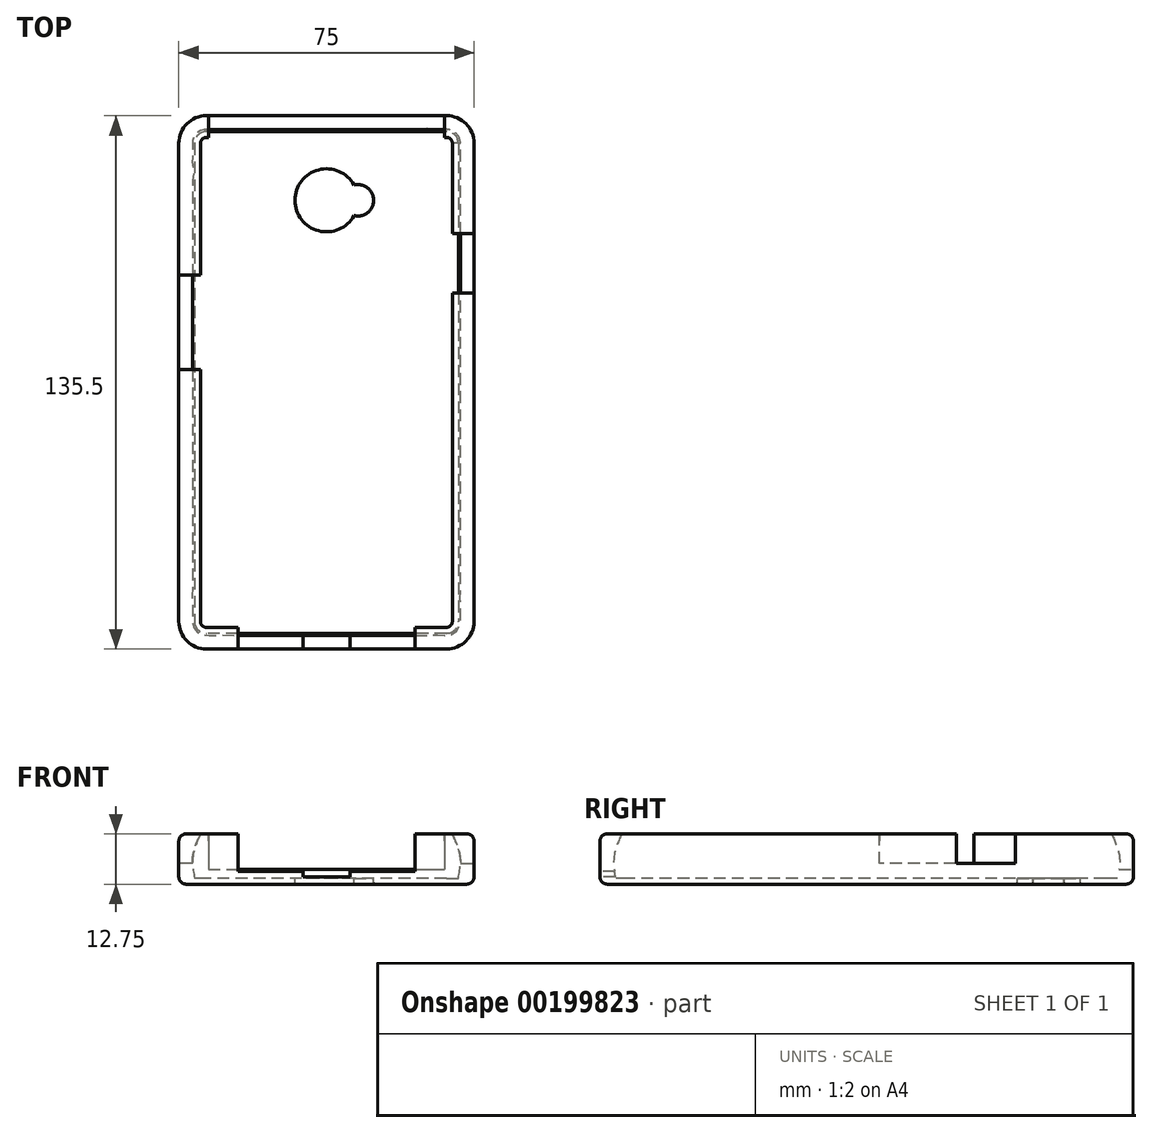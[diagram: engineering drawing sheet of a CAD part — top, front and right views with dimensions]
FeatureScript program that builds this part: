
annotation { "Feature Type Name" : "Feature", "Feature Type Description" : "" }
export const myFeature = defineFeature(function(context is Context, id is Id, definition is map)
    precondition{}
    {
        {
            var Q0;
            Q0=qCreatedBy(makeId("Top.planeOp"),FACE);
            var sketch = newSketch(context, id + "F0", { "sketchPlane" : qUnion([Q0])});
            skLineSegment(sketch, "E0.bottom", {"start": v(30.5, 63.25) * mm, "end": v(-30.5, 63.25) * mm});
            skLineSegment(sketch, "E0.top", {"start": v(30.5, -63.25) * mm, "end": v(-30.5, -63.25) * mm});
            skLineSegment(sketch, "E0.left", {"start": v(33, 60.75) * mm, "end": v(33, -60.75) * mm});
            skLineSegment(sketch, "E0.right", {"start": v(-33, 60.75) * mm, "end": v(-33, -60.75) * mm});
            skPoint(sketch, "E0.middle", {"position": v(0, 0) * mm});
            skPoint(sketch, "E1.visualSharp", {"position": v(-33, 63.25) * mm});
            skArc(sketch, "E1.filletArc", {"start": v(-30.5, 63.25) * mm, "mid": v(-32.27, 62.52) * mm, "end": v(-33, 60.75) * mm});
            skPoint(sketch, "E2.visualSharp", {"position": v(33, 63.25) * mm});
            skArc(sketch, "E2.filletArc", {"start": v(33, 60.75) * mm, "mid": v(32.27, 62.52) * mm, "end": v(30.5, 63.25) * mm});
            skPoint(sketch, "E3.visualSharp", {"position": v(33, -63.25) * mm});
            skArc(sketch, "E3.filletArc", {"start": v(30.5, -63.25) * mm, "mid": v(32.27, -62.52) * mm, "end": v(33, -60.75) * mm});
            skPoint(sketch, "E4.visualSharp", {"position": v(-33, -63.25) * mm});
            skArc(sketch, "E4.filletArc", {"start": v(-33, -60.75) * mm, "mid": v(-32.27, -62.52) * mm, "end": v(-30.5, -63.25) * mm});
            skArc(sketch, "E5.0", {"start": v(37.5, 60.75) * mm, "mid": v(35.45, 65.7) * mm, "end": v(30.5, 67.75) * mm});
            skLineSegment(sketch, "E5.1", {"start": v(37.5, 60.75) * mm, "end": v(37.5, -60.75) * mm});
            skLineSegment(sketch, "E5.2", {"start": v(30.5, 67.75) * mm, "end": v(-30.5, 67.75) * mm});
            skArc(sketch, "E5.3", {"start": v(30.5, -67.75) * mm, "mid": v(35.45, -65.7) * mm, "end": v(37.5, -60.75) * mm});
            skArc(sketch, "E5.4", {"start": v(-30.5, 67.75) * mm, "mid": v(-35.45, 65.7) * mm, "end": v(-37.5, 60.75) * mm});
            skLineSegment(sketch, "E5.5", {"start": v(-37.5, 60.75) * mm, "end": v(-37.5, -60.75) * mm});
            skArc(sketch, "E5.6", {"start": v(-37.5, -60.75) * mm, "mid": v(-35.45, -65.7) * mm, "end": v(-30.5, -67.75) * mm});
            skLineSegment(sketch, "E5.7", {"start": v(30.5, -67.75) * mm, "end": v(-30.5, -67.75) * mm});
            skSolve(sketch);
        }
        {
            var Q0;
            Q0=makeQuery(id+"F0.imprint","IMPRINT",FACE,{"disambiguationData":[TD([[makeQuery(id+"F0.imprint","IMPRINT",EDGE,{"derivedFrom":sQuery(id+"F0.wireOp",EDGE,"E0.bottom")}),-1.0]])]});
            var Q1;
            Q1=makeQuery(id+"F0.imprint","IMPRINT",FACE,{"disambiguationData":[TD([[makeQuery(id+"F0.imprint","IMPRINT",EDGE,{"derivedFrom":sQuery(id+"F0.wireOp",EDGE,"E0.bottom")}),1.0]])]});
            extrude(context, id + "F1", {"entities" : qUnion([Q0, Q1]), "depth" : 12.75 * mm});
        }
        {
            var Q0;
            Q0=qCreatedBy(makeId("Top.planeOp"),FACE);
            cPlane(context, id + "F2", {"entities" : qUnion([Q0]), "cplaneType" : CPlaneType.OFFSET, "offset" : 1.5 * mm, "width" : 150 * mm, "height" : 150 * mm});
        }
        {
            var Q0;
            Q0=qCreatedBy(id+"F2.planeOp",FACE);
            var sketch = newSketch(context, id + "F3", { "sketchPlane" : qUnion([Q0])});
            skArc(sketch, "E6.0", {"start": v(33.5, 60.75) * mm, "mid": v(32.62, 62.87) * mm, "end": v(30.5, 63.75) * mm});
            skLineSegment(sketch, "E6.1", {"start": v(33.5, 60.75) * mm, "end": v(33.5, -60.75) * mm});
            skLineSegment(sketch, "E6.2", {"start": v(30.5, 63.75) * mm, "end": v(-30.5, 63.75) * mm});
            skArc(sketch, "E6.3", {"start": v(30.5, -63.75) * mm, "mid": v(32.62, -62.87) * mm, "end": v(33.5, -60.75) * mm});
            skArc(sketch, "E6.4", {"start": v(-30.5, 63.75) * mm, "mid": v(-32.62, 62.87) * mm, "end": v(-33.5, 60.75) * mm});
            skLineSegment(sketch, "E6.5", {"start": v(-33.5, 60.75) * mm, "end": v(-33.5, -60.75) * mm});
            skArc(sketch, "E6.6", {"start": v(-33.5, -60.75) * mm, "mid": v(-32.62, -62.87) * mm, "end": v(-30.5, -63.75) * mm});
            skLineSegment(sketch, "E6.7", {"start": v(30.5, -63.75) * mm, "end": v(-30.5, -63.75) * mm});
            skSolve(sketch);
        }
        {
            var Q0;
            Q0=qCreatedBy(id+"F2.planeOp",FACE);
            cPlane(context, id + "F4", {"entities" : qUnion([Q0]), "cplaneType" : CPlaneType.OFFSET, "offset" : 5 * mm, "width" : 150 * mm, "height" : 150 * mm});
        }
        {
            var Q0;
            Q0=qCreatedBy(id+"F4.planeOp",FACE);
            var sketch = newSketch(context, id + "F5", { "sketchPlane" : qUnion([Q0])});
            skArc(sketch, "E7.0", {"start": v(34, 60.75) * mm, "mid": v(32.97, 63.22) * mm, "end": v(30.5, 64.25) * mm});
            skLineSegment(sketch, "E7.1", {"start": v(34, 60.75) * mm, "end": v(34, -60.75) * mm});
            skLineSegment(sketch, "E7.2", {"start": v(30.5, 64.25) * mm, "end": v(-30.5, 64.25) * mm});
            skArc(sketch, "E7.3", {"start": v(30.5, -64.25) * mm, "mid": v(32.97, -63.22) * mm, "end": v(34, -60.75) * mm});
            skArc(sketch, "E7.4", {"start": v(-30.5, 64.25) * mm, "mid": v(-32.97, 63.22) * mm, "end": v(-34, 60.75) * mm});
            skLineSegment(sketch, "E7.5", {"start": v(-34, 60.75) * mm, "end": v(-34, -60.75) * mm});
            skArc(sketch, "E7.6", {"start": v(-34, -60.75) * mm, "mid": v(-32.97, -63.22) * mm, "end": v(-30.5, -64.25) * mm});
            skLineSegment(sketch, "E7.7", {"start": v(30.5, -64.25) * mm, "end": v(-30.5, -64.25) * mm});
            skSolve(sketch);
        }
        {
            var Q0;
            Q0=makeQuery(id+"F1.opExtrude","CAP_FACE",FACE,{"disambiguationData":[OSD([sQuery(id+"F0.wireOp",EDGE,"E5.0"),sQuery(id+"F0.wireOp",EDGE,"E5.1"),sQuery(id+"F0.wireOp",EDGE,"E5.2"),sQuery(id+"F0.wireOp",EDGE,"E5.3"),sQuery(id+"F0.wireOp",EDGE,"E5.4"),sQuery(id+"F0.wireOp",EDGE,"E5.5"),sQuery(id+"F0.wireOp",EDGE,"E5.6"),sQuery(id+"F0.wireOp",EDGE,"E5.7")])],"isStart":false});
            var sketch = newSketch(context, id + "F6", { "sketchPlane" : qUnion([Q0])});
            skArc(sketch, "E8.0", {"start": v(32, 60.75) * mm, "mid": v(31.56, 61.81) * mm, "end": v(30.5, 62.25) * mm});
            skLineSegment(sketch, "E8.1", {"start": v(32, 60.75) * mm, "end": v(32, -60.75) * mm});
            skLineSegment(sketch, "E8.2", {"start": v(30.5, 62.25) * mm, "end": v(-30.5, 62.25) * mm});
            skArc(sketch, "E8.3", {"start": v(30.5, -62.25) * mm, "mid": v(31.56, -61.81) * mm, "end": v(32, -60.75) * mm});
            skArc(sketch, "E8.4", {"start": v(-30.5, 62.25) * mm, "mid": v(-31.56, 61.81) * mm, "end": v(-32, 60.75) * mm});
            skLineSegment(sketch, "E8.5", {"start": v(-32, 60.75) * mm, "end": v(-32, -60.75) * mm});
            skArc(sketch, "E8.6", {"start": v(-32, -60.75) * mm, "mid": v(-31.56, -61.81) * mm, "end": v(-30.5, -62.25) * mm});
            skLineSegment(sketch, "E8.7", {"start": v(30.5, -62.25) * mm, "end": v(-30.5, -62.25) * mm});
            skSolve(sketch);
        }
        {
            var Q1;
            Q1=makeQuery(id+"F3.imprint","IMPRINT",FACE,{"disambiguationData":[TD([[makeQuery(id+"F3.imprint","IMPRINT",EDGE,{"derivedFrom":sQuery(id+"F3.wireOp",EDGE,"E6.0")}),1.0]])]});
            var Q2;
            Q2=makeQuery(id+"F5.imprint","IMPRINT",FACE,{"disambiguationData":[TD([[makeQuery(id+"F5.imprint","IMPRINT",EDGE,{"derivedFrom":sQuery(id+"F5.wireOp",EDGE,"E7.0")}),1.0]])]});
            var Q3;
            Q3=makeQuery(id+"F6.imprint","IMPRINT",FACE,{"disambiguationData":[TD([[makeQuery(id+"F6.imprint","IMPRINT",EDGE,{"derivedFrom":sQuery(id+"F6.wireOp",EDGE,"E8.0")}),1.0]])]});
            loft(context, id + "F7", {"operationType" : NewBodyOperationType.REMOVE, "sheetProfilesArray" : [{ "sheetProfileEntities" : qUnion([Q1]) }, { "sheetProfileEntities" : qUnion([Q2]) }, { "sheetProfileEntities" : qUnion([Q3]) }]});
        }
        {
            var Q0;
            Q0=makeQuery(id+"F7.boolean.opBoolean","COPY",FACE,{"derivedFrom":makeQuery(id+"F7.opLoft","CAP_FACE",FACE,{"disambiguationData":[OSD([makeQuery(id+"F3.imprint","IMPRINT",FACE,{"disambiguationData":[TD([[makeQuery(id+"F3.imprint","IMPRINT",EDGE,{"derivedFrom":sQuery(id+"F3.wireOp",EDGE,"E6.0")}),1.0]])]})])],"isStart":true})});
            var sketch = newSketch(context, id + "F8", { "sketchPlane" : qUnion([Q0])});
            skArc(sketch, "E9", {"start": v(7, 50.12) * mm, "mid": v(-8, 46.25) * mm, "end": v(7, 42.38) * mm});
            skArc(sketch, "E10", {"start": v(7, 42.38) * mm, "mid": v(12, 46.25) * mm, "end": v(7, 50.12) * mm});
            skSolve(sketch);
        }
        {
            var Q0;
            Q0=makeQuery(id+"F8.imprint","IMPRINT",FACE,{"disambiguationData":[TD([[makeQuery(id+"F8.imprint","IMPRINT",EDGE,{"derivedFrom":sQuery(id+"F8.wireOp",EDGE,"E9")}),1.0]])]});
            extrude(context, id + "F9", {"entities" : qUnion([Q0]), "operationType" : NewBodyOperationType.REMOVE, "oppositeDirection" : true, "depth" : 5 * mm});
        }
        {
            var Q0;
            Q0=makeQuery(id+"F1.opExtrude","SWEPT_FACE",FACE,{"disambiguationData":[OSD([sQuery(id+"F0.wireOp",EDGE,"E5.5")])]});
            var sketch = newSketch(context, id + "F10", { "sketchPlane" : qUnion([Q0])});
            skLineSegment(sketch, "E11.bottom", {"start": v(-27.25, 5.25) * mm, "end": v(-3.25, 5.25) * mm});
            skLineSegment(sketch, "E11.top", {"start": v(-27.25, 12.75) * mm, "end": v(-3.25, 12.75) * mm});
            skLineSegment(sketch, "E11.left", {"start": v(-27.25, 5.25) * mm, "end": v(-27.25, 12.75) * mm});
            skLineSegment(sketch, "E11.right", {"start": v(-3.25, 5.25) * mm, "end": v(-3.25, 12.75) * mm});
            skSolve(sketch);
        }
        {
            var Q0;
            Q0=makeQuery(id+"F10.imprint","IMPRINT",FACE,{"disambiguationData":[TD([[makeQuery(id+"F10.imprint","IMPRINT",EDGE,{"derivedFrom":sQuery(id+"F10.wireOp",EDGE,"E11.bottom")}),1.0]])]});
            extrude(context, id + "F11", {"entities" : qUnion([Q0]), "operationType" : NewBodyOperationType.REMOVE, "oppositeDirection" : true, "depth" : 6 * mm});
        }
        {
            var Q0;
            Q0=makeQuery(id+"F1.opExtrude","SWEPT_FACE",FACE,{"disambiguationData":[OSD([sQuery(id+"F0.wireOp",EDGE,"E5.1")])]});
            var sketch = newSketch(context, id + "F12", { "sketchPlane" : qUnion([Q0])});
            skLineSegment(sketch, "E12.bottom", {"start": v(37.75, 12.75) * mm, "end": v(22.75, 12.75) * mm});
            skLineSegment(sketch, "E12.top", {"start": v(37.75, 5.25) * mm, "end": v(22.75, 5.25) * mm});
            skLineSegment(sketch, "E12.left", {"start": v(37.75, 12.75) * mm, "end": v(37.75, 5.25) * mm});
            skLineSegment(sketch, "E12.right", {"start": v(22.75, 12.75) * mm, "end": v(22.75, 5.25) * mm});
            skSolve(sketch);
        }
        {
            var Q0;
            Q0=makeQuery(id+"F12.imprint","IMPRINT",FACE,{"disambiguationData":[TD([[makeQuery(id+"F12.imprint","IMPRINT",EDGE,{"derivedFrom":sQuery(id+"F12.wireOp",EDGE,"E12.bottom")}),1.0]])]});
            extrude(context, id + "F13", {"entities" : qUnion([Q0]), "operationType" : NewBodyOperationType.REMOVE, "oppositeDirection" : true, "depth" : 6 * mm});
        }
        {
            var Q0;
            Q0=makeQuery(id+"F1.opExtrude","SWEPT_FACE",FACE,{"disambiguationData":[OSD([sQuery(id+"F0.wireOp",EDGE,"E5.7")])]});
            var sketch = newSketch(context, id + "F14", { "sketchPlane" : qUnion([Q0])});
            skLineSegment(sketch, "E13.bottom", {"start": v(22.5, 12.75) * mm, "end": v(-22.5, 12.75) * mm});
            skLineSegment(sketch, "E13.top", {"start": v(22.5, 3.25) * mm, "end": v(-22.5, 3.25) * mm});
            skLineSegment(sketch, "E13.left", {"start": v(22.5, 12.75) * mm, "end": v(22.5, 3.25) * mm});
            skLineSegment(sketch, "E13.right", {"start": v(-22.5, 12.75) * mm, "end": v(-22.5, 3.25) * mm});
            skPoint(sketch, "E13.middle", {"position": v(0, 8) * mm});
            skSolve(sketch);
        }
        {
            var Q0;
            Q0=makeQuery(id+"F14.imprint","IMPRINT",FACE,{"disambiguationData":[TD([[makeQuery(id+"F14.imprint","IMPRINT",EDGE,{"derivedFrom":sQuery(id+"F14.wireOp",EDGE,"E13.bottom")}),1.0]])]});
            extrude(context, id + "F15", {"entities" : qUnion([Q0]), "operationType" : NewBodyOperationType.REMOVE, "oppositeDirection" : true, "depth" : 15 * mm});
        }
        {
            var Q0;
            Q0=makeQuery(id+"F1.opExtrude","SWEPT_FACE",FACE,{"disambiguationData":[OSD([sQuery(id+"F0.wireOp",EDGE,"E5.2")])]});
            var sketch = newSketch(context, id + "F16", { "sketchPlane" : qUnion([Q0])});
            skLineSegment(sketch, "E14.bottom", {"start": v(30, 12.75) * mm, "end": v(-30, 12.75) * mm});
            skLineSegment(sketch, "E14.top", {"start": v(30, 3.75) * mm, "end": v(-30, 3.75) * mm});
            skLineSegment(sketch, "E14.left", {"start": v(30, 12.75) * mm, "end": v(30, 3.75) * mm});
            skLineSegment(sketch, "E14.right", {"start": v(-30, 12.75) * mm, "end": v(-30, 3.75) * mm});
            skPoint(sketch, "E14.middle", {"position": v(0, 8.25) * mm});
            skSolve(sketch);
        }
        {
            var Q0;
            Q0=makeQuery(id+"F16.imprint","IMPRINT",FACE,{"disambiguationData":[TD([[makeQuery(id+"F16.imprint","IMPRINT",EDGE,{"derivedFrom":sQuery(id+"F16.wireOp",EDGE,"E14.bottom")}),-1.0]])]});
            extrude(context, id + "F17", {"entities" : qUnion([Q0]), "operationType" : NewBodyOperationType.REMOVE, "oppositeDirection" : true, "depth" : 15 * mm});
        }
        {
            var Q0;
            {var subQ0=sQuery(id+"F0.wireOp",EDGE,"E5.0");var subQ1=sQuery(id+"F0.wireOp",EDGE,"E5.1");Q0=makeQuery(id+"F13.boolean.opBoolean","SPLIT",EDGE,{"disambiguationData":[TD([makeQuery(id+"F1.opExtrude","SWEPT_FACE",FACE,{"disambiguationData":[OSD([subQ0])]})])],"derivedFrom":makeQuery(id+"F1.opExtrude","CAP_EDGE",EDGE,{"disambiguationData":[OSD([subQ1])],"isStart":false})});}
            var Q1;
            Q1=makeQuery(id+"F1.opExtrude","CAP_EDGE",EDGE,{"disambiguationData":[OSD([sQuery(id+"F0.wireOp",EDGE,"E5.0")])],"isStart":false});
            var Q2;
            {var subQ0=sQuery(id+"F0.wireOp",EDGE,"E5.0");var subQ1=sQuery(id+"F0.wireOp",EDGE,"E5.2");Q2=makeQuery(id+"F15.boolean.opBoolean","SPLIT",EDGE,{"disambiguationData":[TD([makeQuery(id+"F1.opExtrude","SWEPT_FACE",FACE,{"disambiguationData":[OSD([subQ0])]})])],"derivedFrom":makeQuery(id+"F1.opExtrude","CAP_EDGE",EDGE,{"disambiguationData":[OSD([subQ1])],"isStart":false})});}
            var Q3;
            {var subQ0=sQuery(id+"F0.wireOp",EDGE,"E5.3");var subQ1=sQuery(id+"F0.wireOp",EDGE,"E5.1");Q3=makeQuery(id+"F13.boolean.opBoolean","SPLIT",EDGE,{"disambiguationData":[TD([makeQuery(id+"F1.opExtrude","SWEPT_FACE",FACE,{"disambiguationData":[OSD([subQ0])]})])],"derivedFrom":makeQuery(id+"F1.opExtrude","CAP_EDGE",EDGE,{"disambiguationData":[OSD([subQ1])],"isStart":false})});}
            var Q4;
            Q4=makeQuery(id+"F1.opExtrude","CAP_EDGE",EDGE,{"disambiguationData":[OSD([sQuery(id+"F0.wireOp",EDGE,"E5.3")])],"isStart":false});
            var Q5;
            {var subQ0=sQuery(id+"F0.wireOp",EDGE,"E5.7");var subQ1=sQuery(id+"F0.wireOp",EDGE,"E5.3");Q5=makeQuery(id+"F15.boolean.opBoolean","SPLIT",EDGE,{"disambiguationData":[TD([makeQuery(id+"F1.opExtrude","SWEPT_FACE",FACE,{"disambiguationData":[OSD([subQ1])]})])],"derivedFrom":makeQuery(id+"F1.opExtrude","CAP_EDGE",EDGE,{"disambiguationData":[OSD([subQ0])],"isStart":false})});}
            var Q6;
            {var subQ0=sQuery(id+"F0.wireOp",EDGE,"E5.7");var subQ1=sQuery(id+"F0.wireOp",EDGE,"E5.6");Q6=makeQuery(id+"F15.boolean.opBoolean","SPLIT",EDGE,{"disambiguationData":[TD([makeQuery(id+"F1.opExtrude","SWEPT_FACE",FACE,{"disambiguationData":[OSD([subQ1])]})])],"derivedFrom":makeQuery(id+"F1.opExtrude","CAP_EDGE",EDGE,{"disambiguationData":[OSD([subQ0])],"isStart":false})});}
            var Q7;
            Q7=makeQuery(id+"F1.opExtrude","CAP_EDGE",EDGE,{"disambiguationData":[OSD([sQuery(id+"F0.wireOp",EDGE,"E5.6")])],"isStart":false});
            var Q8;
            {var subQ0=sQuery(id+"F0.wireOp",EDGE,"E5.6");var subQ1=sQuery(id+"F0.wireOp",EDGE,"E5.5");Q8=makeQuery(id+"F11.boolean.opBoolean","SPLIT",EDGE,{"disambiguationData":[TD([makeQuery(id+"F1.opExtrude","SWEPT_FACE",FACE,{"disambiguationData":[OSD([subQ0])]})])],"derivedFrom":makeQuery(id+"F1.opExtrude","CAP_EDGE",EDGE,{"disambiguationData":[OSD([subQ1])],"isStart":false})});}
            var Q9;
            {var subQ0=sQuery(id+"F0.wireOp",EDGE,"E5.5");var subQ1=sQuery(id+"F0.wireOp",EDGE,"E5.4");Q9=makeQuery(id+"F11.boolean.opBoolean","SPLIT",EDGE,{"disambiguationData":[TD([makeQuery(id+"F1.opExtrude","SWEPT_FACE",FACE,{"disambiguationData":[OSD([subQ1])]})])],"derivedFrom":makeQuery(id+"F1.opExtrude","CAP_EDGE",EDGE,{"disambiguationData":[OSD([subQ0])],"isStart":false})});}
            var Q10;
            Q10=makeQuery(id+"F1.opExtrude","CAP_EDGE",EDGE,{"disambiguationData":[OSD([sQuery(id+"F0.wireOp",EDGE,"E5.4")])],"isStart":false});
            var Q11;
            {var subQ0=sQuery(id+"F0.wireOp",EDGE,"E5.4");var subQ1=sQuery(id+"F0.wireOp",EDGE,"E5.2");Q11=makeQuery(id+"F15.boolean.opBoolean","SPLIT",EDGE,{"disambiguationData":[TD([makeQuery(id+"F1.opExtrude","SWEPT_FACE",FACE,{"disambiguationData":[OSD([subQ0])]})])],"derivedFrom":makeQuery(id+"F1.opExtrude","CAP_EDGE",EDGE,{"disambiguationData":[OSD([subQ1])],"isStart":false})});}
            fillet(context, id + "F18", {"entities" : qUnion([Q0, Q1, Q2, Q3, Q4, Q5, Q6, Q7, Q8, Q9, Q10, Q11]), "radius" : 1.8 * mm, "tangentPropagation" : true, "allowEdgeOverflow" : false});
        }
        {
            var Q0;
            Q0=makeQuery(id+"F1.opExtrude","CAP_EDGE",EDGE,{"disambiguationData":[OSD([sQuery(id+"F0.wireOp",EDGE,"E5.2")])],"isStart":true});
            var Q1;
            Q1=makeQuery(id+"F1.opExtrude","CAP_EDGE",EDGE,{"disambiguationData":[OSD([sQuery(id+"F0.wireOp",EDGE,"E5.4")])],"isStart":true});
            var Q2;
            Q2=makeQuery(id+"F1.opExtrude","CAP_EDGE",EDGE,{"disambiguationData":[OSD([sQuery(id+"F0.wireOp",EDGE,"E5.5")])],"isStart":true});
            var Q3;
            Q3=makeQuery(id+"F1.opExtrude","CAP_EDGE",EDGE,{"disambiguationData":[OSD([sQuery(id+"F0.wireOp",EDGE,"E5.0")])],"isStart":true});
            var Q4;
            Q4=makeQuery(id+"F1.opExtrude","CAP_EDGE",EDGE,{"disambiguationData":[OSD([sQuery(id+"F0.wireOp",EDGE,"E5.1")])],"isStart":true});
            var Q5;
            Q5=makeQuery(id+"F1.opExtrude","CAP_EDGE",EDGE,{"disambiguationData":[OSD([sQuery(id+"F0.wireOp",EDGE,"E5.3")])],"isStart":true});
            var Q6;
            Q6=makeQuery(id+"F1.opExtrude","CAP_EDGE",EDGE,{"disambiguationData":[OSD([sQuery(id+"F0.wireOp",EDGE,"E5.7")])],"isStart":true});
            var Q7;
            Q7=makeQuery(id+"F1.opExtrude","CAP_EDGE",EDGE,{"disambiguationData":[OSD([sQuery(id+"F0.wireOp",EDGE,"E5.6")])],"isStart":true});
            fillet(context, id + "F19", {"entities" : qUnion([Q0, Q1, Q2, Q3, Q4, Q5, Q6, Q7]), "radius" : 1.8 * mm, "tangentPropagation" : true, "allowEdgeOverflow" : false});
        }
        {
            var Q0;
            Q0=makeQuery(id+"F9.boolean.opBoolean","INTERSECT",EDGE,{"derivedFrom":[makeQuery(id+"F1.opExtrude","CAP_FACE",FACE,{"disambiguationData":[OSD([sQuery(id+"F0.wireOp",EDGE,"E5.0"),sQuery(id+"F0.wireOp",EDGE,"E5.1"),sQuery(id+"F0.wireOp",EDGE,"E5.2"),sQuery(id+"F0.wireOp",EDGE,"E5.3"),sQuery(id+"F0.wireOp",EDGE,"E5.4"),sQuery(id+"F0.wireOp",EDGE,"E5.5"),sQuery(id+"F0.wireOp",EDGE,"E5.6"),sQuery(id+"F0.wireOp",EDGE,"E5.7")])],"isStart":true}),makeQuery(id+"F9.opExtrude","SWEPT_FACE",FACE,{"disambiguationData":[OSD([sQuery(id+"F8.wireOp",EDGE,"E9")])]})]});
            var Q1;
            Q1=makeQuery(id+"F1.opExtrude","CAP_FACE",FACE,{"disambiguationData":[OSD([sQuery(id+"F0.wireOp",EDGE,"E5.0"),sQuery(id+"F0.wireOp",EDGE,"E5.1"),sQuery(id+"F0.wireOp",EDGE,"E5.2"),sQuery(id+"F0.wireOp",EDGE,"E5.3"),sQuery(id+"F0.wireOp",EDGE,"E5.4"),sQuery(id+"F0.wireOp",EDGE,"E5.5"),sQuery(id+"F0.wireOp",EDGE,"E5.6"),sQuery(id+"F0.wireOp",EDGE,"E5.7")])],"isStart":true});
            fillet(context, id + "F20", {"entities" : qUnion([Q0, Q1]), "radius" : 0.25 * mm, "tangentPropagation" : true, "allowEdgeOverflow" : false});
        }
        {
            var Q0;
            Q0=makeQuery(id+"F1.opExtrude","SWEPT_FACE",FACE,{"disambiguationData":[OSD([sQuery(id+"F0.wireOp",EDGE,"E5.7")])]});
            var sketch = newSketch(context, id + "F21", { "sketchPlane" : qUnion([Q0])});
            skLineSegment(sketch, "E15.bottom", {"start": v(6, 1.8) * mm, "end": v(-6, 1.8) * mm});
            skLineSegment(sketch, "E15.top", {"start": v(6, 6.8) * mm, "end": v(-6, 6.8) * mm});
            skLineSegment(sketch, "E15.left", {"start": v(6, 1.8) * mm, "end": v(6, 6.8) * mm});
            skLineSegment(sketch, "E15.right", {"start": v(-6, 1.8) * mm, "end": v(-6, 6.8) * mm});
            skPoint(sketch, "E15.middle", {"position": v(0, 4.3) * mm});
            skSolve(sketch);
        }
        {
            var Q0;
            {var subQ0=sQuery(id+"F21.wireOp",EDGE,"E15.bottom");Q0=makeQuery(id+"F21.imprint","IMPRINT",FACE,{"disambiguationData":[TD([[makeQuery(id+"F21.imprint","IMPRINT",EDGE,{"derivedFrom":subQ0}),1.0]])]});}
            extrude(context, id + "F22", {"entities" : qUnion([Q0]), "operationType" : NewBodyOperationType.REMOVE, "oppositeDirection" : true, "depth" : 10 * mm});
        }
    });
